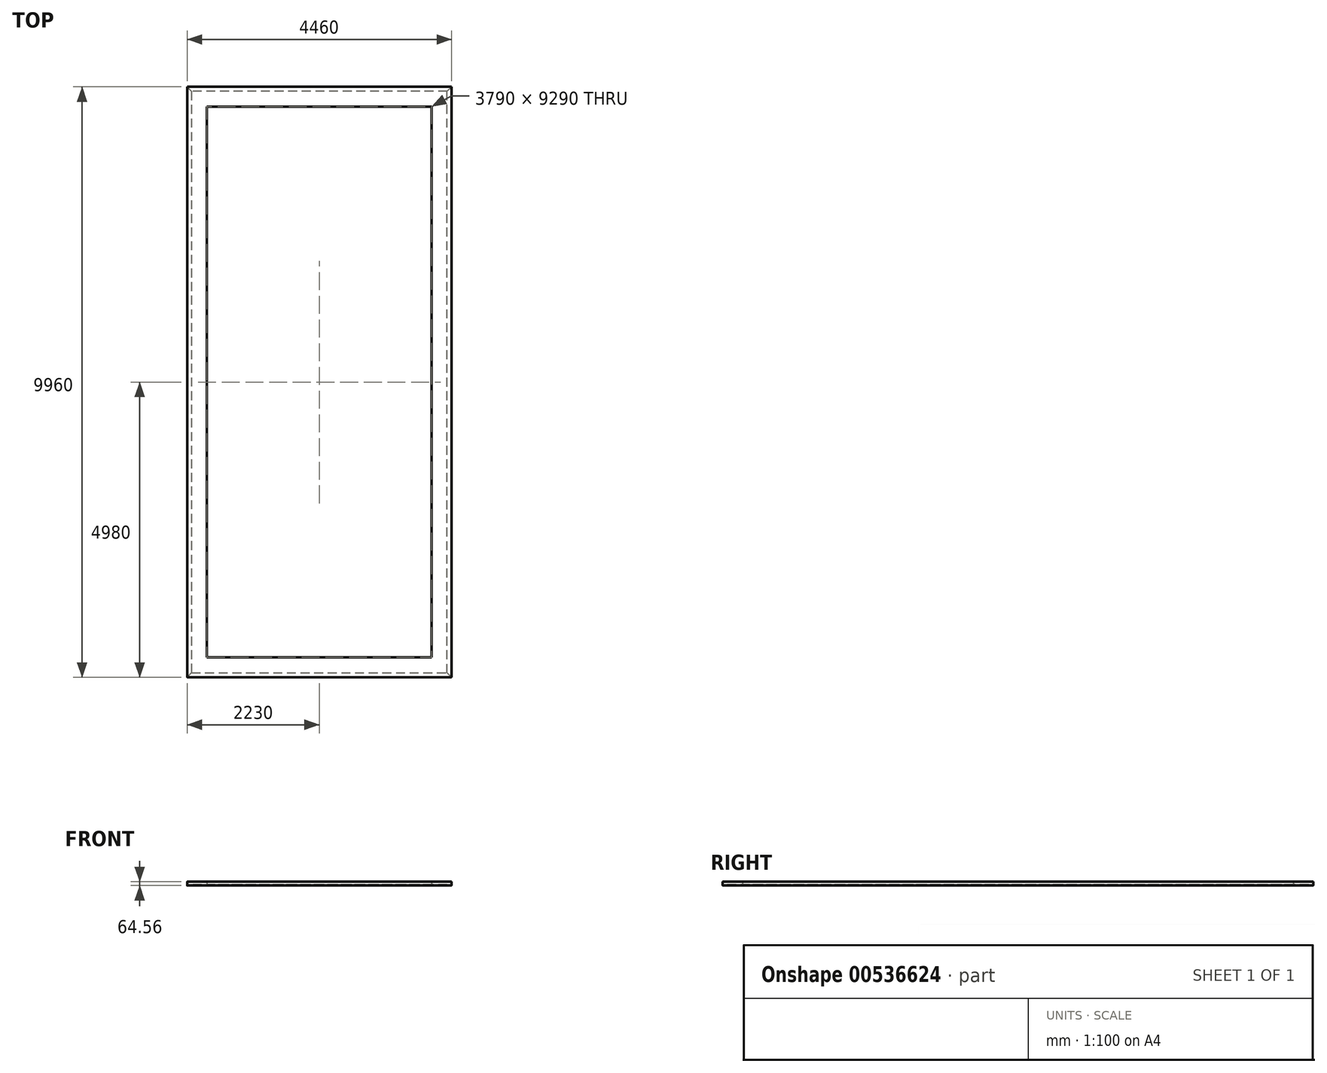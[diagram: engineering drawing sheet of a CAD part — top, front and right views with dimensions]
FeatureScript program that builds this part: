
annotation { "Feature Type Name" : "Feature", "Feature Type Description" : "" }
export const myFeature = defineFeature(function(context is Context, id is Id, definition is map)
    precondition{}
    {
        {
            var Q0;
            Q0=qCreatedBy(makeId("Top.planeOp"),FACE);
            var sketch = newSketch(context, id + "F0", { "sketchPlane" : qUnion([Q0])});
            skLineSegment(sketch, "E0.bottom", {"start": v(2230, 4980) * mm, "end": v(-2230, 4980) * mm});
            skLineSegment(sketch, "E0.top", {"start": v(2230, -4980) * mm, "end": v(-2230, -4980) * mm});
            skLineSegment(sketch, "E0.left", {"start": v(2230, 4980) * mm, "end": v(2230, -4980) * mm});
            skLineSegment(sketch, "E0.right", {"start": v(-2230, 4980) * mm, "end": v(-2230, -4980) * mm});
            skPoint(sketch, "E0.middle", {"position": v(0, 0) * mm});
            skLineSegment(sketch, "E1", {"start": v(0, 0) * mm, "end": v(-2230, 0) * mm, "construction": true});
            skSolve(sketch);
        }
        {
            var Q0;
            Q0=sQuery(id+"F0.wireOp",EDGE,"E1");
            cPlane(context, id + "F1", {"entities" : qUnion([Q0]), "cplaneType" : CPlaneType.LINE_ANGLE, "offset" : 25 * mm, "angle" : 0 * degree, "width" : 150 * mm, "height" : 150 * mm});
        }
        {
            var Q0;
            Q0=qCreatedBy(id+"F1.planeOp",FACE);
            var sketch = newSketch(context, id + "F2", { "sketchPlane" : qUnion([Q0])});
            skLineSegment(sketch, "E2.0", {"start": v(0, 0) * mm, "end": v(-2230, 0) * mm, "construction": true});
            skLineSegment(sketch, "E3", {"start": v(-2228, 0) * mm, "end": v(-1895, 0) * mm});
            skLineSegment(sketch, "E4", {"start": v(-2230, -2) * mm, "end": v(-2230, -62.56) * mm});
            skLineSegment(sketch, "E5", {"start": v(-2227.6, -64.52) * mm, "end": v(-2156.6, -50.32) * mm});
            skLineSegment(sketch, "E6", {"start": v(-2155, -48.36) * mm, "end": v(-2155, -37) * mm});
            skLineSegment(sketch, "E7", {"start": v(-2153, -35) * mm, "end": v(-2097, -35) * mm});
            skLineSegment(sketch, "E8", {"start": v(-2095, -37) * mm, "end": v(-2095, -48) * mm});
            skLineSegment(sketch, "E9", {"start": v(-2093, -50) * mm, "end": v(-1895, -50) * mm});
            skLineSegment(sketch, "E10", {"start": v(-1895, -50) * mm, "end": v(-1895, 0) * mm});
            skPoint(sketch, "E11.visualSharp", {"position": v(-2155, -35) * mm});
            skArc(sketch, "E11.filletArc", {"start": v(-2153, -35) * mm, "mid": v(-2154.41, -35.59) * mm, "end": v(-2155, -37) * mm});
            skPoint(sketch, "E12.visualSharp", {"position": v(-2095, -35) * mm});
            skArc(sketch, "E12.filletArc", {"start": v(-2095, -37) * mm, "mid": v(-2095.59, -35.59) * mm, "end": v(-2097, -35) * mm});
            skPoint(sketch, "E13.visualSharp", {"position": v(-2095, -50) * mm});
            skArc(sketch, "E13.filletArc", {"start": v(-2095, -48) * mm, "mid": v(-2094.41, -49.41) * mm, "end": v(-2093, -50) * mm});
            skPoint(sketch, "E14.visualSharp", {"position": v(-2155, -50) * mm});
            skArc(sketch, "E14.filletArc", {"start": v(-2156.6, -50.32) * mm, "mid": v(-2155.45, -49.63) * mm, "end": v(-2155, -48.36) * mm});
            skPoint(sketch, "E15.visualSharp", {"position": v(-2230, 0) * mm});
            skArc(sketch, "E15.filletArc", {"start": v(-2228, 0) * mm, "mid": v(-2229.41, -0.59) * mm, "end": v(-2230, -2) * mm});
            skPoint(sketch, "E16.visualSharp", {"position": v(-2230, -65) * mm});
            skArc(sketch, "E16.filletArc", {"start": v(-2230, -62.56) * mm, "mid": v(-2229.27, -64.1) * mm, "end": v(-2227.6, -64.52) * mm});
            skSolve(sketch);
        }
        {
            var Q0;
            Q0=makeQuery(id+"F2.imprint","IMPRINT",FACE,{"disambiguationData":[TD([[makeQuery(id+"F2.imprint","IMPRINT",EDGE,{"derivedFrom":sQuery(id+"F2.wireOp",EDGE,"E3")}),-1.0]])]});
            var Q1;
            Q1=sQuery(id+"F0.wireOp",EDGE,"E0.right");
            var Q2;
            Q2=sQuery(id+"F0.wireOp",EDGE,"E0.bottom");
            var Q3;
            Q3=sQuery(id+"F0.wireOp",EDGE,"E0.left");
            var Q4;
            Q4=sQuery(id+"F0.wireOp",EDGE,"E0.top");
            sweep(context, id + "F3", {"profiles" : qUnion([Q0]), "path" : qUnion([Q1, Q2, Q3, Q4])});
        }
        {
            var Q0;
            Q0=makeQuery(id+"F3.opSweep","SWEPT_FACE",FACE,{"disambiguationData":[OSD([sQuery(id+"F0.wireOp",EDGE,"E0.right"),sQuery(id+"F2.wireOp",EDGE,"E3")])]});
            var sketch = newSketch(context, id + "F4", { "sketchPlane" : qUnion([Q0])});
            skLineSegment(sketch, "E17.0", {"start": v(-1895, 4645) * mm, "end": v(1895, 4645) * mm});
            skLineSegment(sketch, "E18.0", {"start": v(1895, 4645) * mm, "end": v(1895, -4645) * mm});
            skLineSegment(sketch, "E19.0", {"start": v(-1895, -4645) * mm, "end": v(-1895, 4645) * mm});
            skLineSegment(sketch, "E20.0", {"start": v(1895, -4645) * mm, "end": v(-1895, -4645) * mm});
            skSolve(sketch);
        }
        {
            var Q0;
            Q0=makeQuery(id+"F4.imprint","IMPRINT",FACE,{"disambiguationData":[TD([[makeQuery(id+"F4.imprint","IMPRINT",EDGE,{"derivedFrom":sQuery(id+"F4.wireOp",EDGE,"E17.0")}),-1.0]])]});
            extrude(context, id + "F5", {"entities" : qUnion([Q0]), "operationType" : NewBodyOperationType.ADD, "oppositeDirection" : true, "depth" : 50 * mm});
        }
    });
